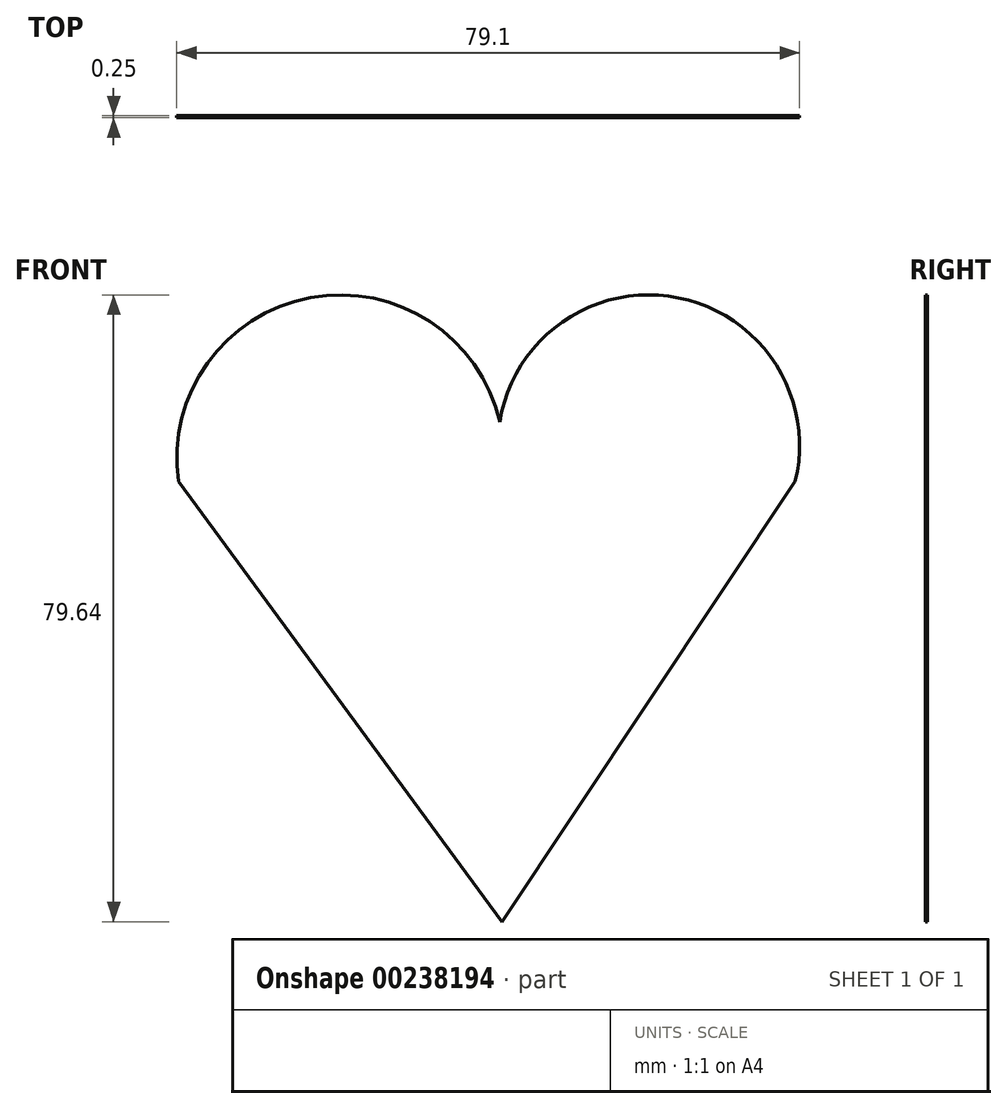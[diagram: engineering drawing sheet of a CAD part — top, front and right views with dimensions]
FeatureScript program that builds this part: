
annotation { "Feature Type Name" : "Feature", "Feature Type Description" : "" }
export const myFeature = defineFeature(function(context is Context, id is Id, definition is map)
    precondition{}
    {
        {
            var Q0;
            Q0=qCreatedBy(makeId("Front.planeOp"),FACE);
            var sketch = newSketch(context, id + "F0", { "sketchPlane" : qUnion([Q0])});
            skLineSegment(sketch, "E0", {"start": v(0, -55.92) * mm, "end": v(-41.13, 0) * mm});
            skLineSegment(sketch, "E1", {"start": v(0, -55.92) * mm, "end": v(37.21, 0) * mm});
            skArc(sketch, "E2", {"start": v(0, 0) * mm, "mid": v(-20.57, 23.72) * mm, "end": v(-41.13, 0) * mm});
            skArc(sketch, "E3", {"start": v(37.21, 0) * mm, "mid": v(18.6, 23.72) * mm, "end": v(0, 0) * mm});
            skSolve(sketch);
        }
        {
            var Q0;
            Q0 = qSketchRegion(id + "F0", true);
            extrude(context, id + "F1", {"entities" : qUnion([Q0]), "depth" : 0.25 * mm});
        }
    });
